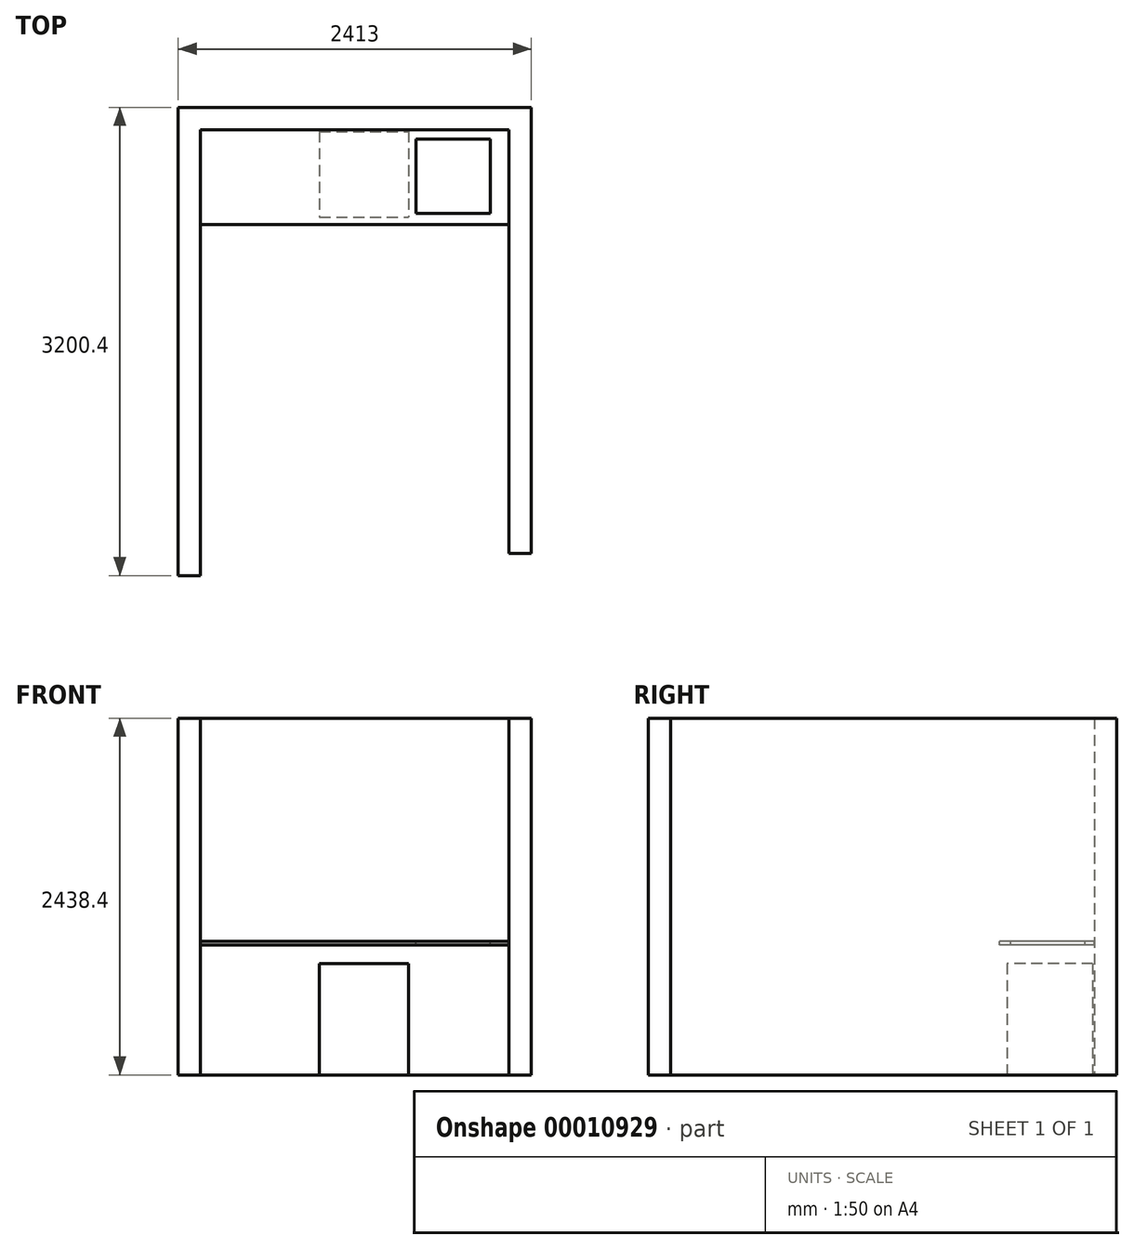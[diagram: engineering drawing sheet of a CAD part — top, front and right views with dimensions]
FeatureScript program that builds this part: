
annotation { "Feature Type Name" : "Feature", "Feature Type Description" : "" }
export const myFeature = defineFeature(function(context is Context, id is Id, definition is map)
    precondition{}
    {
        {
            var Q0;
            Q0=qCreatedBy(makeId("Top.planeOp"),FACE);
            cPlane(context, id + "F0", {"entities" : qUnion([Q0]), "cplaneType" : CPlaneType.OFFSET, "offset" : 914.4 * mm, "width" : 152.4 * mm, "height" : 152.4 * mm});
        }
        {
            var Q0;
            Q0=qCreatedBy(makeId("Top.planeOp"),FACE);
            var sketch = newSketch(context, id + "F1", { "sketchPlane" : qUnion([Q0])});
            skLineSegment(sketch, "E0", {"start": v(0, 0) * mm, "end": v(0, -3048) * mm});
            skLineSegment(sketch, "E1", {"start": v(0, -3048) * mm, "end": v(-152.4, -3048) * mm});
            skLineSegment(sketch, "E2", {"start": v(-152.4, -3048) * mm, "end": v(-152.4, 152.4) * mm});
            skLineSegment(sketch, "E3", {"start": v(-152.4, 152.4) * mm, "end": v(2260.6, 152.4) * mm});
            skLineSegment(sketch, "E4", {"start": v(2260.6, 152.4) * mm, "end": v(2260.6, -2895.6) * mm});
            skLineSegment(sketch, "E5", {"start": v(2260.6, -2895.6) * mm, "end": v(2108.2, -2895.6) * mm});
            skLineSegment(sketch, "E6", {"start": v(2108.2, -2895.6) * mm, "end": v(2108.2, 0) * mm});
            skLineSegment(sketch, "E7", {"start": v(2108.2, 0) * mm, "end": v(0, 0) * mm});
            skSolve(sketch);
        }
        {
            var Q0;
            Q0=makeQuery(id+"F1.imprint","IMPRINT",FACE,{"disambiguationData":[TD([[makeQuery(id+"F1.imprint","IMPRINT",EDGE,{"derivedFrom":sQuery(id+"F1.wireOp",EDGE,"E0")}),-1.0]])]});
            extrude(context, id + "F2", {"entities" : qUnion([Q0]), "depth" : 2438.4 * mm});
        }
        {
            var Q0;
            Q0=qCreatedBy(id+"F0.planeOp",FACE);
            var sketch = newSketch(context, id + "F3", { "sketchPlane" : qUnion([Q0])});
            skLineSegment(sketch, "E8.bottom", {"start": v(0, 0) * mm, "end": v(2108.2, 0) * mm});
            skLineSegment(sketch, "E8.top", {"start": v(0, -647.7) * mm, "end": v(2108.2, -647.7) * mm});
            skLineSegment(sketch, "E8.left", {"start": v(0, 0) * mm, "end": v(0, -647.7) * mm});
            skLineSegment(sketch, "E8.right", {"start": v(2108.2, 0) * mm, "end": v(2108.2, -647.7) * mm});
            skLineSegment(sketch, "E9.bottom", {"start": v(1473.2, -63.5) * mm, "end": v(1981.2, -63.5) * mm});
            skLineSegment(sketch, "E9.top", {"start": v(1473.2, -571.5) * mm, "end": v(1981.2, -571.5) * mm});
            skLineSegment(sketch, "E9.left", {"start": v(1473.2, -63.5) * mm, "end": v(1473.2, -571.5) * mm});
            skLineSegment(sketch, "E9.right", {"start": v(1981.2, -63.5) * mm, "end": v(1981.2, -571.5) * mm});
            skSolve(sketch);
        }
        {
            var Q0;
            Q0=makeQuery(id+"F3.imprint","IMPRINT",FACE,{"disambiguationData":[TD([[makeQuery(id+"F3.imprint","IMPRINT",EDGE,{"derivedFrom":sQuery(id+"F3.wireOp",EDGE,"E8.bottom")}),-1.0]])]});
            extrude(context, id + "F4", {"entities" : qUnion([Q0]), "oppositeDirection" : true, "depth" : 25.4 * mm});
        }
        {
            var Q0;
            Q0=qCreatedBy(makeId("Top.planeOp"),FACE);
            var sketch = newSketch(context, id + "F5", { "sketchPlane" : qUnion([Q0])});
            skLineSegment(sketch, "E10.bottom", {"start": v(812.8, -12.7) * mm, "end": v(1422.4, -12.7) * mm});
            skLineSegment(sketch, "E10.top", {"start": v(812.8, -596.9) * mm, "end": v(1422.4, -596.9) * mm});
            skLineSegment(sketch, "E10.left", {"start": v(812.8, -12.7) * mm, "end": v(812.8, -596.9) * mm});
            skLineSegment(sketch, "E10.right", {"start": v(1422.4, -12.7) * mm, "end": v(1422.4, -596.9) * mm});
            skSolve(sketch);
        }
        {
            var Q0;
            Q0=makeQuery(id+"F5.imprint","IMPRINT",FACE,{"disambiguationData":[TD([[makeQuery(id+"F5.imprint","IMPRINT",EDGE,{"derivedFrom":sQuery(id+"F5.wireOp",EDGE,"E10.bottom")}),-1.0]])]});
            extrude(context, id + "F6", {"entities" : qUnion([Q0]), "depth" : 762 * mm});
        }
    });
